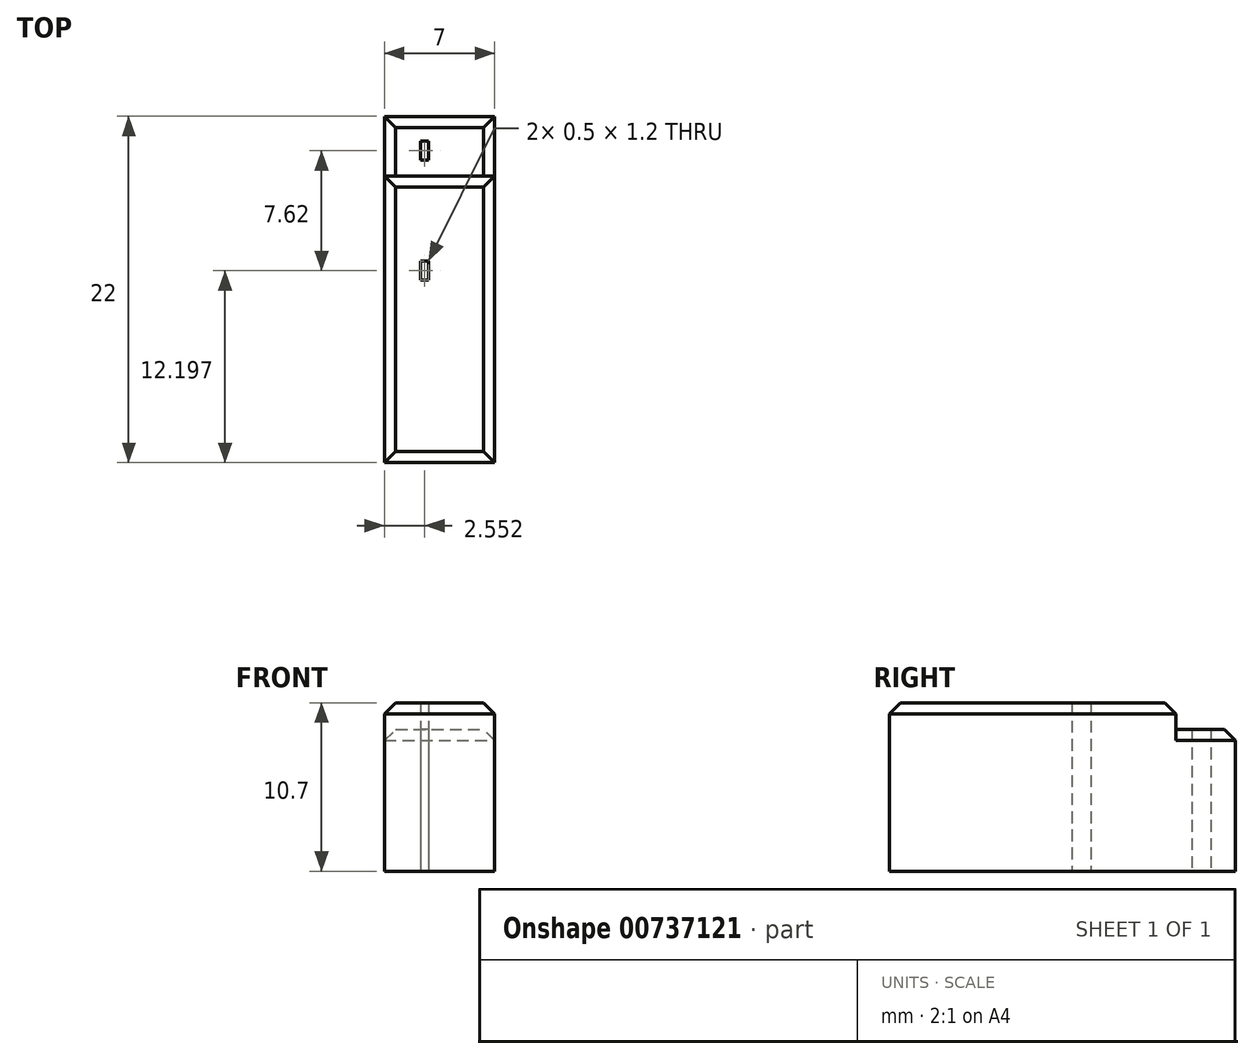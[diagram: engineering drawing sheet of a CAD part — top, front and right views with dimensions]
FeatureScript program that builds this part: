
annotation { "Feature Type Name" : "Feature", "Feature Type Description" : "" }
export const myFeature = defineFeature(function(context is Context, id is Id, definition is map)
    precondition{}
    {
        {
            var Q0;
            Q0=qCreatedBy(makeId("Top.planeOp"),FACE);
            var sketch = newSketch(context, id + "F0", { "sketchPlane" : qUnion([Q0])});
            skLineSegment(sketch, "E0.bottom", {"start": v(-58.1, 5.1) * mm, "end": v(-51.1, 5.1) * mm});
            skLineSegment(sketch, "E0.top", {"start": v(-58.1, -13.1) * mm, "end": v(-51.1, -13.1) * mm});
            skLineSegment(sketch, "E0.left", {"start": v(-58.1, 5.1) * mm, "end": v(-58.1, -13.1) * mm});
            skLineSegment(sketch, "E0.right", {"start": v(-51.1, 5.1) * mm, "end": v(-51.1, -13.1) * mm});
            skLineSegment(sketch, "E1.top", {"start": v(-58.1, 8.9) * mm, "end": v(-51.1, 8.9) * mm});
            skLineSegment(sketch, "E1.left", {"start": v(-58.1, 5.1) * mm, "end": v(-58.1, 8.9) * mm});
            skLineSegment(sketch, "E1.right", {"start": v(-51.1, 5.1) * mm, "end": v(-51.1, 8.9) * mm});
            skCircle(sketch, "E2", {"center": v(-55.55, -11.05) * mm, "radius": 1.02 * mm, "construction": true});
            skCircle(sketch, "E3", {"center": v(-55.55, -0.9) * mm, "radius": 1.3 * mm, "construction": true});
            skCircle(sketch, "E4", {"center": v(-55.55, 6.73) * mm, "radius": 1.1 * mm, "construction": true});
            skLineSegment(sketch, "E5.bottom", {"start": v(-55.3, -0.3) * mm, "end": v(-55.8, -0.3) * mm});
            skLineSegment(sketch, "E5.top", {"start": v(-55.3, -1.5) * mm, "end": v(-55.8, -1.5) * mm});
            skLineSegment(sketch, "E5.left", {"start": v(-55.3, -0.3) * mm, "end": v(-55.3, -1.5) * mm});
            skLineSegment(sketch, "E5.right", {"start": v(-55.8, -0.3) * mm, "end": v(-55.8, -1.5) * mm});
            skLineSegment(sketch, "E6.bottom", {"start": v(-55.3, 6.13) * mm, "end": v(-55.8, 6.13) * mm});
            skLineSegment(sketch, "E6.top", {"start": v(-55.3, 7.33) * mm, "end": v(-55.8, 7.33) * mm});
            skLineSegment(sketch, "E6.left", {"start": v(-55.3, 6.13) * mm, "end": v(-55.3, 7.33) * mm});
            skLineSegment(sketch, "E6.right", {"start": v(-55.8, 6.13) * mm, "end": v(-55.8, 7.33) * mm});
            skLineSegment(sketch, "E7.bottom", {"start": v(-55.3, -11.65) * mm, "end": v(-55.8, -11.65) * mm, "construction": true});
            skLineSegment(sketch, "E7.top", {"start": v(-55.3, -10.45) * mm, "end": v(-55.8, -10.45) * mm, "construction": true});
            skLineSegment(sketch, "E7.left", {"start": v(-55.3, -11.65) * mm, "end": v(-55.3, -10.45) * mm, "construction": true});
            skLineSegment(sketch, "E7.right", {"start": v(-55.8, -11.65) * mm, "end": v(-55.8, -10.45) * mm, "construction": true});
            skSolve(sketch);
        }
        {
            var Q0;
            Q0=makeQuery(id+"F0.imprint","IMPRINT",FACE,{"disambiguationData":[TD([[makeQuery(id+"F0.imprint","IMPRINT",EDGE,{"derivedFrom":sQuery(id+"F0.wireOp",EDGE,"E0.bottom")}),1.0]])]});
            extrude(context, id + "F1", {"entities" : qUnion([Q0]), "depth" : 9 * mm, "offsetDistance" : 25 * mm});
        }
        {
            var Q0;
            Q0=makeQuery(id+"F0.imprint","IMPRINT",FACE,{"disambiguationData":[TD([[makeQuery(id+"F0.imprint","IMPRINT",EDGE,{"derivedFrom":sQuery(id+"F0.wireOp",EDGE,"E0.top")}),1.0]])]});
            extrude(context, id + "F2", {"entities" : qUnion([Q0]), "operationType" : NewBodyOperationType.ADD, "depth" : 10.7 * mm, "offsetDistance" : 25 * mm});
        }
        {
            var Q0;
            Q0=makeQuery(id+"F1.opExtrude","CAP_EDGE",EDGE,{"disambiguationData":[OSD([sQuery(id+"F0.wireOp",EDGE,"E1.top")])],"isStart":false});
            chamfer(context, id + "F3", {"entities" : qUnion([Q0]), "width" : 0.7 * mm, "tangentPropagation" : true});
        }
        {
            var Q0;
            Q0=makeQuery(id+"F2.opExtrude","CAP_EDGE",EDGE,{"disambiguationData":[OSD([sQuery(id+"F0.wireOp",EDGE,"E0.bottom")])],"isStart":false});
            var Q1;
            Q1=makeQuery(id+"F2.opExtrude","CAP_EDGE",EDGE,{"disambiguationData":[OSD([sQuery(id+"F0.wireOp",EDGE,"E0.right")])],"isStart":false});
            var Q2;
            Q2=makeQuery(id+"F2.opExtrude","CAP_EDGE",EDGE,{"disambiguationData":[OSD([sQuery(id+"F0.wireOp",EDGE,"E0.left")])],"isStart":false});
            var Q3;
            Q3=makeQuery(id+"F2.opExtrude","CAP_EDGE",EDGE,{"disambiguationData":[OSD([sQuery(id+"F0.wireOp",EDGE,"E0.top")])],"isStart":false});
            var Q4;
            Q4=makeQuery(id+"F1.opExtrude","CAP_EDGE",EDGE,{"disambiguationData":[OSD([sQuery(id+"F0.wireOp",EDGE,"E1.left")])],"isStart":false});
            var Q5;
            Q5=makeQuery(id+"F1.opExtrude","CAP_EDGE",EDGE,{"disambiguationData":[OSD([sQuery(id+"F0.wireOp",EDGE,"E1.right")])],"isStart":false});
            chamfer(context, id + "F4", {"entities" : qUnion([Q0, Q1, Q2, Q3, Q4, Q5]), "width" : 0.7 * mm, "tangentPropagation" : true});
        }
    });
